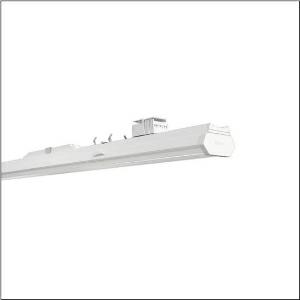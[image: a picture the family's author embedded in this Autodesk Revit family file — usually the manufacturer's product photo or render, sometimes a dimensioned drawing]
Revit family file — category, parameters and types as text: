
# Revit family: licross_r__21_protected_mo_52tp11dn4a5g_5e2b
name_source: partatom
category: Lighting Fixtures
units: mm (PartAtom-declared; Revit-internal decimal feet)

## family parameters
Cut with Voids When Loaded = No
Host = Face
Light Source = No
Part Type = Normal
Room Calculation Point = No
Round Connector Dimension = Use Diameter
Shared = No

## types (1)
- --- (1 x LED, 10650 lm, 62 W, 4000K)
    Apparent Load = 62 VA
    CIE Flux Codes = 83 94 98 100 100
    Color Rendering = 80
    Color Temperature = 4000K
    Default Elevation = 1800 mm
    Description = Licross® 21 Protected MO, luminaire insert, of sheet steel, galvanised, coil coated, white, length: 1.500mm, width: 90mm, height: 103mm, LED rated luminous flux: 10.650lm, light colour: 840, control gear: DALI 2, with plug, 5-pole, with phase selection, mains connection: 220..240V, AC, 50/60Hz, rated input power: 62W, halogen-free wiring, primary light control with lens, of plastic, primary optical cover: cover, of PMMA, light emission: direct distribution, primary light characteristic: symmetric, protection rating (complete): IP64, insulation class (complete): insulation class I (protective earthing), certification: CE, ENEC, VDE, UKCA, protection symbol: D if used in an environment with conductive dust loads with corresponding accessories, impact resistance: IK06, permissible ambient temperature for indoor applications: -25..+35°C, corresponds to IFS (International Featured Standards) requirements for safety and quality in the food industry, reducing of maximum allowable ambient temperature of 5°C with ceiling mounting, LABS conformity tested according to VDMA 24364:2018-05, packaging unit: 1 piece
    Height = 92 mm
    Lamp = 1 x LED
    Lamp Light Flux = 10650 lm
    Lamp Power = 62 W
    Lamp count = 1
    Length = 1500 mm
    Luminous efficacy = 172 lm/W
    Manufacturer = Siteco
    ModVariant = No
    Model = 52TP11DN4A5G
    Mounting Place = Ceiling
    Mounting Type = Pendant
    Number of Poles = 1
    OnlyDefault = Yes
    Power Factor = 1
    Product Name = Licross® 21 Protected MO
    Product group = luminaire insert
    ProductGroupID = 902
    Protection Class = Protection class I
    Protection Degree = IP 64
    RLX_Detail_Level = 1
    RLX_Emergency_Light_Flux = 0 lm
    RLX_Emergency_Type = 0
    RLX_Emergency_Type_DB = No
    RlxData = <blob elided: 24005 chars, md5=285014b5>
    Socket = socket
    Standby Power = 0 W
    System Light Flux = 10650 lm
    System Power = 62 W
    Type Comments = factory setting: luminous flux: 100 % | dim-lin: 254 | 418 mA
    Type Image = l_1256148.jpg
    URL = http://relux.com
    VarID = @adj_128216
    Voltage = 0 V
    Weight = 0.00 kg
    Width = 88 mm

## geometry (parser evidence)
native form markers: Blend x4, Sweep x11
no freeform markers — native parametric forms only
